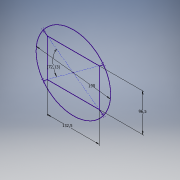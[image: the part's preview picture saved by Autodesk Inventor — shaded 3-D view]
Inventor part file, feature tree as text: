
AUTODESK INVENTOR PART (.ipt)
format: ipt  version: 2016 (Build 200138000, 138)  size: 89,600 bytes
history: native  units: mm
features: sketch x1
ambient origin geometry x8: Origin, YZ Plane, XZ Plane, XY Plane, X Axis, Y Axis, Z Axis, Center Point
feature tree (1):
  sketch  "Sketch2"  dims[d10=132.5mm d11=96.5mm d12=190.0mm d13=12.589382mm]
